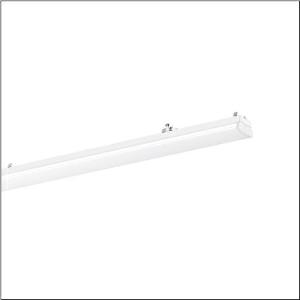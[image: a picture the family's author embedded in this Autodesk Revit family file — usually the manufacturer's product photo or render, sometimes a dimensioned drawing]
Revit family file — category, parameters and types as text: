
# Revit family: licross_11_recessed_opal_mo_51tl1ddv4e5g
name_source: partatom
category: Lighting Fixtures
units: mm (PartAtom-declared; Revit-internal decimal feet)

## family parameters
Cut with Voids When Loaded = No
Host = Face
Light Source = No
Part Type = Normal
Room Calculation Point = No
Round Connector Dimension = Use Diameter
Shared = No

## types (1)
- --- (1 x LED, 14560 lm, 84.1 W, 4000K)
    Apparent Load = 84 VA
    CIE Flux Codes = 44 73 91 87 100
    Color Rendering = 80
    Color Temperature = 4000K
    Default Elevation = 1800 mm
    Description = Licross 11 recessed opal MO, luminaire insert, of sheet steel, coil coated, white, length: 2.250mm, width: 76mm, height: 87mm, LED rated luminous flux: 14.560lm, light colour: 840, SDCM (Standard Deviation of Colour Matching)MacAdam ≤ 2 SDCM (initial), control gear: DALI 2, with plug, 5-pole, with phase selection, mains connection: 220..240V, AC, 50/60Hz, rated input power: 84W, internal wiring halogen-free, primary optical cover: cover, of PMMA, light emission: direct with ceiling illumination distribution, primary light characteristic: symmetric, protection rating (complete): IP40, insulation class (complete): insulation class I (protective earthing), certification: CE, ENEC, VDE, UKCA, protection symbol: D if used in an environment without relevant dust loads with corresponding accessories, impact resistance: IK06, permissible ambient temperature for indoor applications: -25..+35°C, corresponds to IFS (International Featured Standards) requirements for safety and quality in the food industry, reducing of maximum allowable ambient temperature of 5°C with ceiling mounting, LABS conformity tested according to VDMA 24364:2018-05, The light source and the operating device comply with the requirements of the Ecodesign Regulation (EU) 2019/2020 and are replaceable in accordance with this regulation, packaging unit: 1 piece
    Height = 83 mm
    Lamp = 1 x LED
    Lamp Light Flux = 14560 lm
    Lamp Power = 84.1 W
    Lamp count = 1
    Length = 2250 mm
    Luminous efficacy = 173 lm/W
    Manufacturer = Siteco
    ModVariant = No
    Model = 51TL1DDV4E5G
    Mounting Place = Ceiling
    Mounting Type = Pendant
    Number of Poles = 1
    OnlyDefault = Yes
    Power Factor = 1
    Product Name = Licross 11 recessed opal MO
    Product group = luminaire insert | ceiling pendant
    ProductGroupID = 901
    Protection Class = Protection class I
    Protection Degree = IP 40
    RLX_Detail_Level = 1
    RLX_Emergency_Light_Flux = 0 lm
    RLX_Emergency_Type = 0
    RLX_Emergency_Type_DB = No
    RlxData = <blob elided: 26965 chars, md5=953ccc16>
    Socket = socket
    Standby Power = 0 W
    System Light Flux = 14560 lm
    System Power = 84 W
    Type Comments = factory setting: luminous flux: 100 % | dim-lin: 254 | 378 mA
    Type Image = l_1313666.jpg
    URL = http://relux.com
    VarID = @adj_085773
    Voltage = 0 V
    Weight = 0.00 kg
    Width = 76 mm

## geometry (parser evidence)
native form markers: Blend x4, Sweep x12
no freeform markers — native parametric forms only
